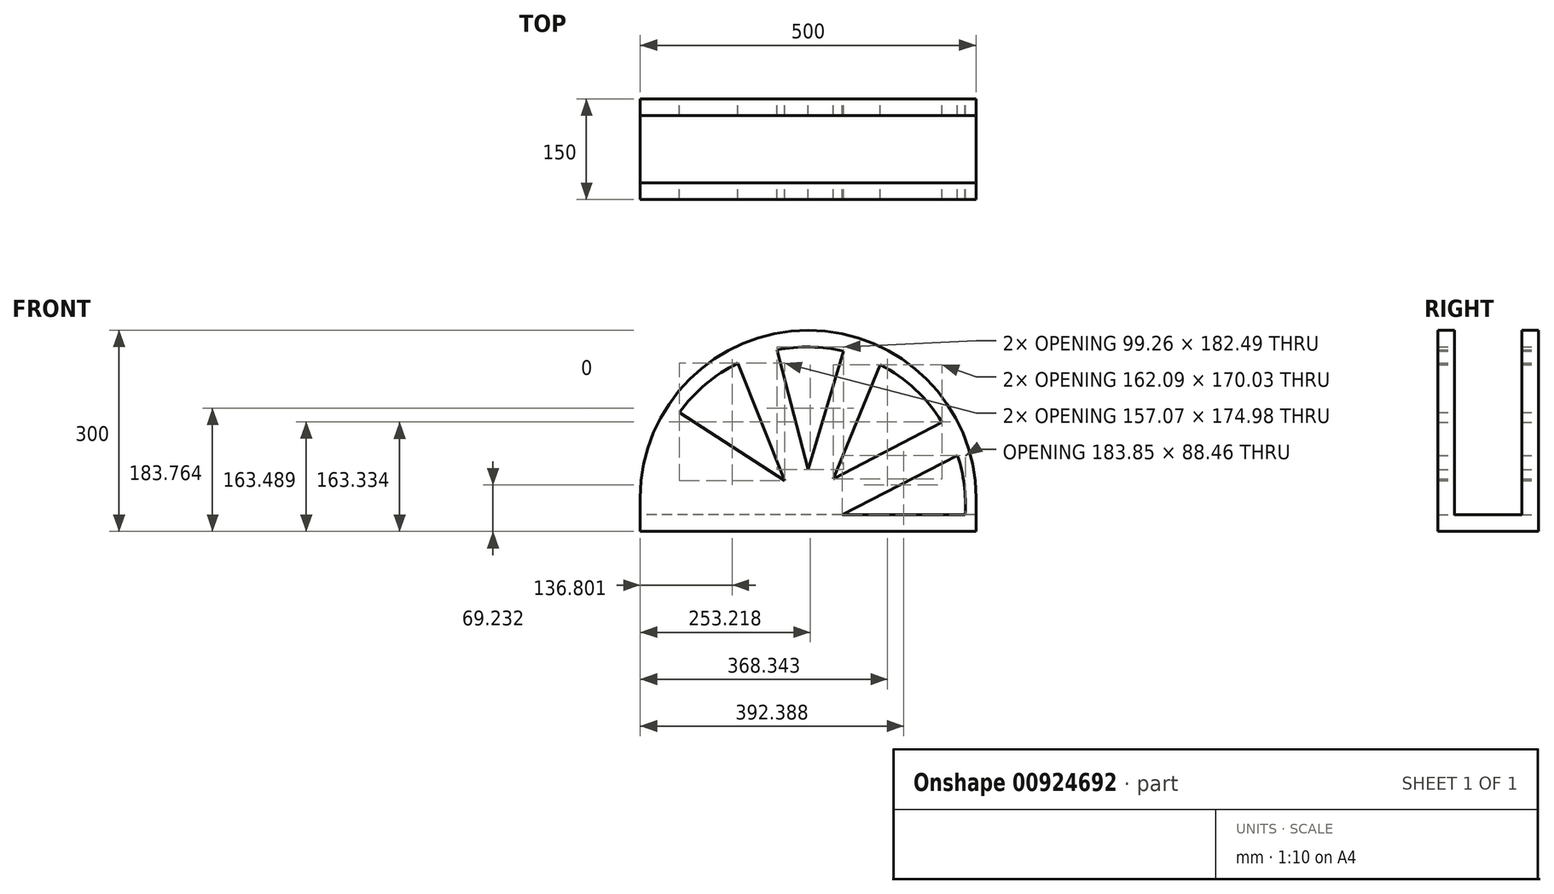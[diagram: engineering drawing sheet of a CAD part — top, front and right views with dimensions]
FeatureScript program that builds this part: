
annotation { "Feature Type Name" : "Feature", "Feature Type Description" : "" }
export const myFeature = defineFeature(function(context is Context, id is Id, definition is map)
    precondition{}
    {
        {
            var Q0;
            Q0=qCreatedBy(makeId("Front.planeOp"),FACE);
            var sketch = newSketch(context, id + "F0", { "sketchPlane" : qUnion([Q0])});
            skLineSegment(sketch, "E0.bottom", {"start": v(250, -25) * mm, "end": v(-250, -25) * mm});
            skLineSegment(sketch, "E0.left", {"start": v(250, -25) * mm, "end": v(250, 25) * mm});
            skLineSegment(sketch, "E0.right", {"start": v(-250, -25) * mm, "end": v(-250, 25) * mm});
            skPoint(sketch, "E0.middle", {"position": v(0, 0) * mm});
            skArc(sketch, "E1", {"start": v(250, 25) * mm, "mid": v(0, 275) * mm, "end": v(-250, 25) * mm});
            skSolve(sketch);
        }
        {
            var Q0;
            Q0=makeQuery(id+"F0.imprint","IMPRINT",FACE,{"disambiguationData":[TD([[makeQuery(id+"F0.imprint","IMPRINT",EDGE,{"derivedFrom":sQuery(id+"F0.wireOp",EDGE,"E0.bottom")}),-1.0]])]});
            extrude(context, id + "F1", {"entities" : qUnion([Q0]), "oppositeDirection" : true, "depth" : 150 * mm, "offsetDistance" : 25 * mm});
        }
        {
            var Q0;
            Q0=makeQuery(id+"F1.opExtrude","SWEPT_FACE",FACE,{"disambiguationData":[OSD([sQuery(id+"F0.wireOp",EDGE,"E0.right")])]});
            var sketch = newSketch(context, id + "F2", { "sketchPlane" : qUnion([Q0])});
            skLineSegment(sketch, "E2.bottom", {"start": v(-125, 0) * mm, "end": v(-25, 0) * mm});
            skLineSegment(sketch, "E2.top", {"start": v(-125, 322.66) * mm, "end": v(-25, 322.66) * mm});
            skLineSegment(sketch, "E2.left", {"start": v(-125, 0) * mm, "end": v(-125, 322.66) * mm});
            skLineSegment(sketch, "E2.right", {"start": v(-25, 0) * mm, "end": v(-25, 322.66) * mm});
            skSolve(sketch);
        }
        {
            var Q0;
            {var subQ0=sQuery(id+"F2.wireOp",EDGE,"E2.top");Q0=makeQuery(id+"F2.imprint","IMPRINT",FACE,{"disambiguationData":[TD([[makeQuery(id+"F2.imprint","IMPRINT",EDGE,{"derivedFrom":subQ0}),-1.0]])]});}
            var Q1;
            {var subQ0=sQuery(id+"F2.wireOp",EDGE,"E2.bottom");Q1=makeQuery(id+"F2.imprint","IMPRINT",FACE,{"disambiguationData":[TD([[makeQuery(id+"F2.imprint","IMPRINT",EDGE,{"derivedFrom":subQ0}),1.0]])]});}
            extrude(context, id + "F3", {"entities" : qUnion([Q0, Q1]), "operationType" : NewBodyOperationType.REMOVE, "oppositeDirection" : true, "depth" : 10000 * mm, "offsetDistance" : 25 * mm});
        }
        {
            var Q0;
            Q0=makeQuery(id+"F1.opExtrude","CAP_FACE",FACE,{"disambiguationData":[OSD([sQuery(id+"F0.wireOp",EDGE,"E0.bottom"),sQuery(id+"F0.wireOp",EDGE,"E0.left"),sQuery(id+"F0.wireOp",EDGE,"E0.right"),sQuery(id+"F0.wireOp",EDGE,"E1")])],"isStart":false});
            var sketch = newSketch(context, id + "F4", { "sketchPlane" : qUnion([Q0])});
            skArc(sketch, "E3", {"start": v(235.95, 0) * mm, "mid": v(1.03, 250.05) * mm, "end": v(-233.88, 0) * mm});
            skLineSegment(sketch, "E4", {"start": v(-233.88, 0) * mm, "end": v(235.95, 0) * mm});
            skLineSegment(sketch, "E5", {"start": v(-222.48, 88.46) * mm, "end": v(-50.46, 0) * mm});
            skLineSegment(sketch, "E6", {"start": v(-199.39, 138.1) * mm, "end": v(-37.3, 53.48) * mm});
            skLineSegment(sketch, "E7", {"start": v(-37.3, 53.48) * mm, "end": v(-107.56, 223.5) * mm});
            skLineSegment(sketch, "E8", {"start": v(-52.85, 243.8) * mm, "end": v(0, 67.52) * mm});
            skLineSegment(sketch, "E9", {"start": v(0, 67.52) * mm, "end": v(46.41, 245.64) * mm});
            skLineSegment(sketch, "E10", {"start": v(105.04, 225.83) * mm, "end": v(34.67, 50.84) * mm});
            skLineSegment(sketch, "E11", {"start": v(34.67, 50.84) * mm, "end": v(191.73, 152.65) * mm});
            skLineSegment(sketch, "E12", {"start": v(221.6, 101.74) * mm, "end": v(38.18, 0) * mm});
            skSolve(sketch);
        }
        {
            var Q0;
            {var subQ3=sQuery(id+"F4.wireOp",EDGE,"E5");Q0=makeQuery(id+"F4.imprint","IMPRINT",FACE,{"disambiguationData":[TD([[makeQuery(id+"F4.imprint","IMPRINT",EDGE,{"derivedFrom":subQ3}),-1.0]])]});}
            var Q1;
            {var subQ0=sQuery(id+"F4.wireOp",EDGE,"E6");Q1=makeQuery(id+"F4.imprint","IMPRINT",FACE,{"disambiguationData":[TD([[makeQuery(id+"F4.imprint","IMPRINT",EDGE,{"derivedFrom":subQ0}),1.0]])]});}
            var Q2;
            {var subQ0=sQuery(id+"F4.wireOp",EDGE,"E8");Q2=makeQuery(id+"F4.imprint","IMPRINT",FACE,{"disambiguationData":[TD([[makeQuery(id+"F4.imprint","IMPRINT",EDGE,{"derivedFrom":subQ0}),1.0]])]});}
            var Q3;
            {var subQ0=sQuery(id+"F4.wireOp",EDGE,"E10");Q3=makeQuery(id+"F4.imprint","IMPRINT",FACE,{"disambiguationData":[TD([[makeQuery(id+"F4.imprint","IMPRINT",EDGE,{"derivedFrom":subQ0}),1.0]])]});}
            var Q4;
            {var subQ0=sQuery(id+"F4.wireOp",EDGE,"E4");var subQ1=sQuery(id+"F4.wireOp",EDGE,"E3");var subQ2=makeQuery(id+"F4.imprint","INTERSECT",VERTEX,{"disambiguationData":[OD(0.0)],"derivedFrom":[subQ1,subQ0]});Q4=makeQuery(id+"F4.imprint","IMPRINT",FACE,{"disambiguationData":[TD([[makeQuery(id+"F4.imprint","IMPRINT",EDGE,{"disambiguationData":[TD([[subQ2,-1.0]])],"derivedFrom":subQ1}),1.0]])]});}
            extrude(context, id + "F5", {"entities" : qUnion([Q0, Q1, Q2, Q3, Q4]), "operationType" : NewBodyOperationType.REMOVE, "oppositeDirection" : true, "depth" : 10000 * mm, "offsetDistance" : 25 * mm});
        }
    });
